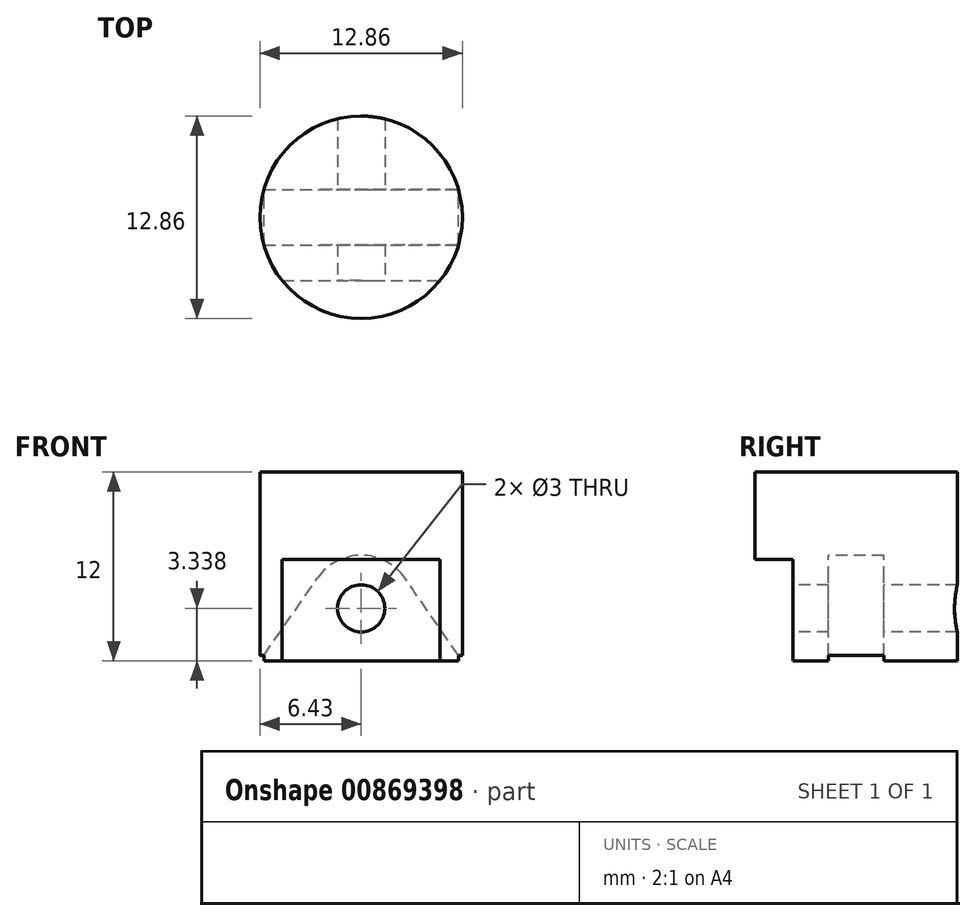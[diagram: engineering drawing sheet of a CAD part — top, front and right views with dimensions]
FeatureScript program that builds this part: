
annotation { "Feature Type Name" : "Feature", "Feature Type Description" : "" }
export const myFeature = defineFeature(function(context is Context, id is Id, definition is map)
    precondition{}
    {
        {
            var Q0;
            Q0=qCreatedBy(makeId("Top.planeOp"),FACE);
            var sketch = newSketch(context, id + "F0", { "sketchPlane" : qUnion([Q0])});
            skCircle(sketch, "E0", {"center": v(0, 0) * mm, "radius": 6.42 * mm});
            skSolve(sketch);
        }
        {
            var Q0;
            Q0 = qSketchRegion(id + "F0", true);
            extrude(context, id + "F1", {"entities" : qUnion([Q0]), "oppositeDirection" : true, "depth" : 12 * mm, "offsetDistance" : 25 * mm});
        }
        {
            var Q0;
            Q0=qCreatedBy(makeId("Front.planeOp"),FACE);
            var sketch = newSketch(context, id + "F2", { "sketchPlane" : qUnion([Q0])});
            skCircle(sketch, "E1", {"center": v(0, -8.66) * mm, "radius": 1.5 * mm});
            skSolve(sketch);
        }
        {
            var Q0;
            Q0 = qSketchRegion(id + "F2", true);
            extrude(context, id + "F3", {"entities" : qUnion([Q0]), "operationType" : NewBodyOperationType.REMOVE, "endBound" : BoundingType.SYMMETRIC, "oppositeDirection" : true, "depth" : 25 * mm, "offsetDistance" : 25 * mm});
        }
        {
            var Q0;
            Q0=qCreatedBy(makeId("Front.planeOp"),FACE);
            var sketch = newSketch(context, id + "F4", { "sketchPlane" : qUnion([Q0])});
            skArc(sketch, "E2", {"start": v(2.77, -6.74) * mm, "mid": v(0, -5.29) * mm, "end": v(-2.77, -6.74) * mm});
            skLineSegment(sketch, "E3.0", {"start": v(-6.42, -12) * mm, "end": v(6.42, -12) * mm});
            skLineSegment(sketch, "E4", {"start": v(6.43, -12) * mm, "end": v(2.77, -6.74) * mm});
            skLineSegment(sketch, "E5", {"start": v(-6.43, -12) * mm, "end": v(-2.77, -6.74) * mm});
            skSolve(sketch);
        }
        {
            var Q0;
            Q0 = qSketchRegion(id + "F4", true);
            extrude(context, id + "F5", {"entities" : qUnion([Q0]), "operationType" : NewBodyOperationType.REMOVE, "endBound" : BoundingType.SYMMETRIC, "oppositeDirection" : true, "depth" : 3.5 * mm, "offsetDistance" : 25 * mm});
        }
        {
            var Q0;
            Q0=qCreatedBy(makeId("Right.planeOp"),FACE);
            var sketch = newSketch(context, id + "F6", { "sketchPlane" : qUnion([Q0])});
            skLineSegment(sketch, "E6", {"start": v(-6.42, -12) * mm, "end": v(-6.42, -5.56) * mm});
            skLineSegment(sketch, "E7", {"start": v(-4.03, -12) * mm, "end": v(-4.03, -5.56) * mm});
            skLineSegment(sketch, "E8", {"start": v(-4.03, -5.56) * mm, "end": v(-6.42, -5.56) * mm});
            skLineSegment(sketch, "E9", {"start": v(-6.42, -7.16) * mm, "end": v(-4.03, -7.16) * mm});
            skLineSegment(sketch, "E10", {"start": v(-4.03, -10.16) * mm, "end": v(-6.42, -10.16) * mm});
            skPoint(sketch, "E11.orphan", {"position": v(-6.42, -12) * mm});
            skPoint(sketch, "E12.0.start.orphan", {"position": v(-1.75, -12) * mm});
            skPoint(sketch, "E13.orphan", {"position": v(0, -10.16) * mm});
            skPoint(sketch, "E14.orphan", {"position": v(0, -7.16) * mm});
            skLineSegment(sketch, "E15", {"start": v(-6.42, -10.16) * mm, "end": v(-6.42, -12) * mm});
            skLineSegment(sketch, "E16", {"start": v(-4.03, -12) * mm, "end": v(-6.42, -12) * mm});
            skLineSegment(sketch, "E17.0", {"start": v(-1.75, -11.65) * mm, "end": v(-1.75, -12) * mm});
            skLineSegment(sketch, "E18.0", {"start": v(1.75, -11.65) * mm, "end": v(1.75, -12) * mm});
            skLineSegment(sketch, "E19", {"start": v(-1.75, -11.65) * mm, "end": v(1.75, -11.65) * mm});
            skLineSegment(sketch, "E20", {"start": v(-1.75, -12) * mm, "end": v(1.75, -12) * mm});
            skSolve(sketch);
        }
        {
            var Q0;
            {var subQ0=sQuery(id+"F6.wireOp",EDGE,"E10");var subQ6=makeQuery(id+"F6.imprint","IMPRINT",EDGE,{"derivedFrom":subQ0});var subQ7=sQuery(id+"F6.wireOp",EDGE,"E9");var subQ10=makeQuery(id+"F6.imprint","IMPRINT",EDGE,{"derivedFrom":subQ7});var subQ11=sQuery(id+"F6.wireOp",EDGE,"E8");Q0=qUnion([makeQuery(id+"F6.imprint","IMPRINT",FACE,{"disambiguationData":[TD([[makeQuery(id+"F6.imprint","IMPRINT",EDGE,{"derivedFrom":sQuery(id+"F6.wireOp",EDGE,"E17.0")}),1.0]])]}),makeQuery(id+"F6.imprint","IMPRINT",FACE,{"disambiguationData":[TD([[makeQuery(id+"F6.imprint","IMPRINT",EDGE,{"derivedFrom":subQ11}),1.0]])]}),makeQuery(id+"F6.imprint","IMPRINT",FACE,{"disambiguationData":[TD([[subQ10,-1.0]])]}),makeQuery(id+"F6.imprint","IMPRINT",FACE,{"disambiguationData":[TD([[subQ6,1.0]])]})]);}
            extrude(context, id + "F7", {"entities" : qUnion([Q0]), "operationType" : NewBodyOperationType.REMOVE, "endBound" : BoundingType.SYMMETRIC, "oppositeDirection" : true, "depth" : 25 * mm, "offsetDistance" : 25 * mm});
        }
    });
